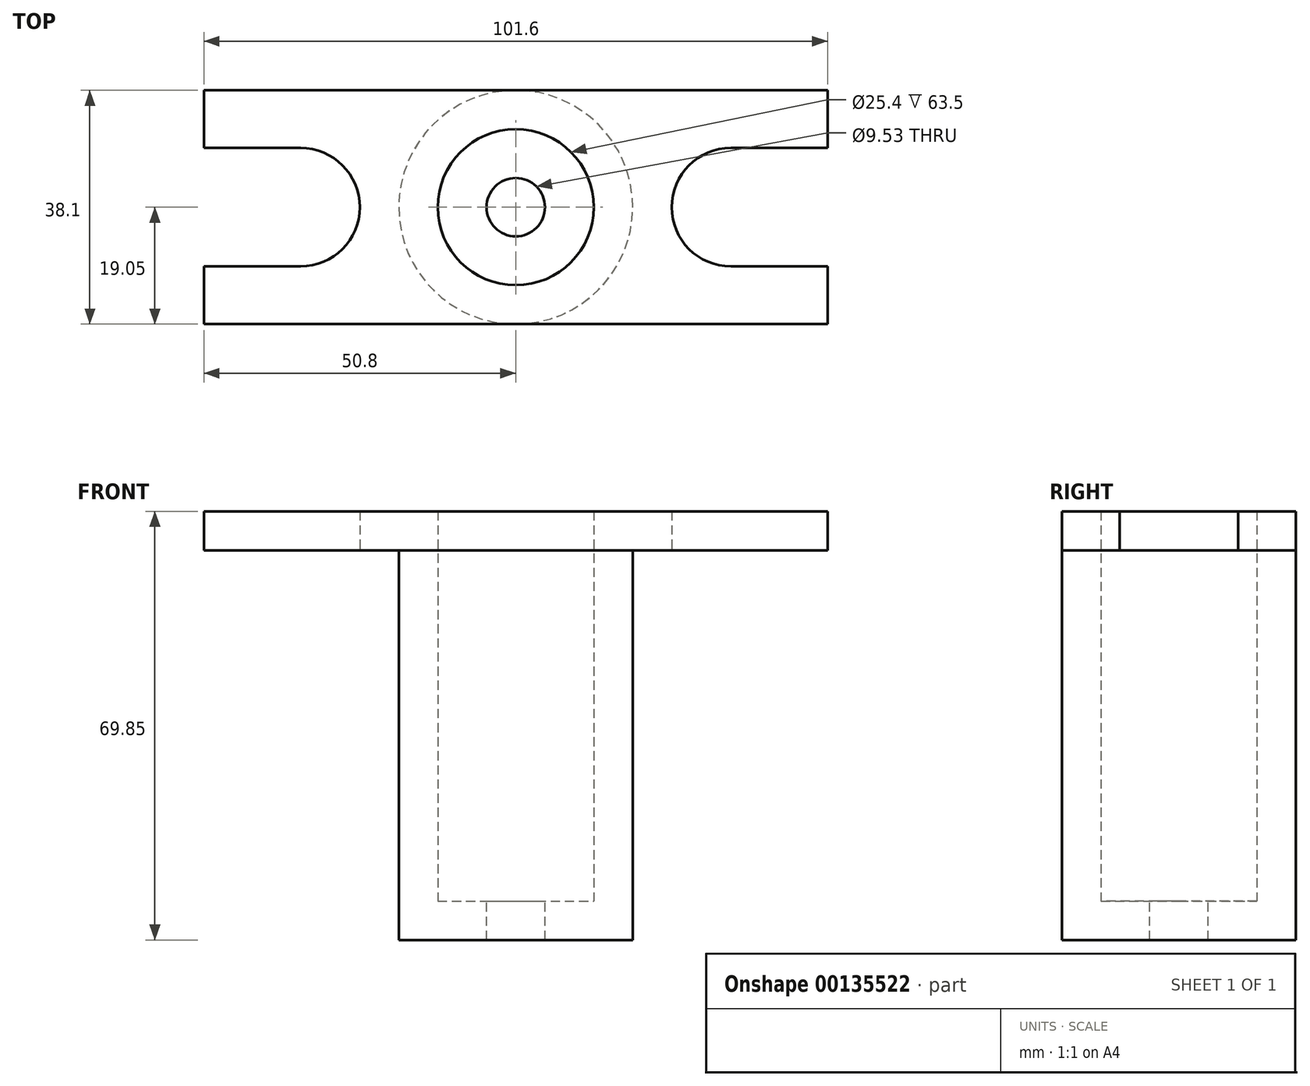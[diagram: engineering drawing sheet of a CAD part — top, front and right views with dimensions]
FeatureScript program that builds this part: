
annotation { "Feature Type Name" : "Feature", "Feature Type Description" : "" }
export const myFeature = defineFeature(function(context is Context, id is Id, definition is map)
    precondition{}
    {
        {
            var Q0;
            Q0=qCreatedBy(makeId("Top.planeOp"),FACE);
            var sketch = newSketch(context, id + "F0", { "sketchPlane" : qUnion([Q0])});
            skLineSegment(sketch, "E0.bottom", {"start": v(0, 0) * mm, "end": v(101.6, 0) * mm});
            skLineSegment(sketch, "E0.top", {"start": v(0, 38.1) * mm, "end": v(101.6, 38.1) * mm});
            skLineSegment(sketch, "E0.left", {"start": v(0, 0) * mm, "end": v(0, 9.4) * mm});
            skLineSegment(sketch, "E0.right", {"start": v(101.6, 0) * mm, "end": v(101.6, 9.4) * mm});
            skLineSegment(sketch, "E1", {"start": v(50.8, 38.1) * mm, "end": v(50.8, 0) * mm, "construction": true});
            skLineSegment(sketch, "E2", {"start": v(0, 19.05) * mm, "end": v(101.6, 19.05) * mm, "construction": true});
            skCircle(sketch, "E3", {"center": v(50.8, 19.05) * mm, "radius": 12.7 * mm});
            skCircle(sketch, "E4", {"center": v(50.8, 19.05) * mm, "radius": 19.05 * mm});
            skCircle(sketch, "E5", {"center": v(50.8, 19.05) * mm, "radius": 4.76 * mm});
            skLineSegment(sketch, "E6", {"start": v(101.6, 28.7) * mm, "end": v(85.85, 28.7) * mm});
            skLineSegment(sketch, "E7", {"start": v(101.6, 9.4) * mm, "end": v(85.85, 9.4) * mm});
            skArc(sketch, "E8", {"start": v(85.85, 28.7) * mm, "mid": v(76.2, 19.05) * mm, "end": v(85.85, 9.4) * mm});
            skLineSegment(sketch, "E9.MirrorCS", {"start": v(0, 28.7) * mm, "end": v(15.75, 28.7) * mm});
            skArc(sketch, "E10.MirrorCS", {"start": v(15.75, 28.7) * mm, "mid": v(25.4, 19.05) * mm, "end": v(15.75, 9.4) * mm});
            skLineSegment(sketch, "E11.MirrorCS", {"start": v(0, 9.4) * mm, "end": v(15.75, 9.4) * mm});
            skLineSegment(sketch, "E12.trimOffspring", {"start": v(0, 28.7) * mm, "end": v(0, 38.1) * mm});
            skLineSegment(sketch, "E13.trimOffspring", {"start": v(101.6, 28.7) * mm, "end": v(101.6, 38.1) * mm});
            skSolve(sketch);
        }
        {
            var Q0;
            Q0 = qSketchRegion(id + "F0", true);
            extrude(context, id + "F1", {"entities" : qUnion([Q0]), "depth" : 6.35 * mm});
        }
        {
            var Q0;
            Q0=makeQuery(id+"F0.imprint","IMPRINT",FACE,{"disambiguationData":[TD([[makeQuery(id+"F0.imprint","IMPRINT",EDGE,{"derivedFrom":sQuery(id+"F0.wireOp",EDGE,"E3")}),-1.0]])]});
            extrude(context, id + "F2", {"entities" : qUnion([Q0]), "operationType" : NewBodyOperationType.ADD, "oppositeDirection" : true, "depth" : 63.5 * mm});
        }
        {
            var Q0;
            Q0=makeQuery(id+"F2.opExtrude","CAP_FACE",FACE,{"disambiguationData":[OSD([sQuery(id+"F0.wireOp",EDGE,"E3"),sQuery(id+"F0.wireOp",EDGE,"E4")])],"isStart":false});
            var sketch = newSketch(context, id + "F3", { "sketchPlane" : qUnion([Q0])});
            skCircle(sketch, "E14.0", {"center": v(50.8, -19.05) * mm, "radius": 19.05 * mm});
            skSolve(sketch);
        }
        {
            var Q0;
            Q0 = qSketchRegion(id + "F3", true);
            extrude(context, id + "F4", {"entities" : qUnion([Q0]), "operationType" : NewBodyOperationType.ADD, "oppositeDirection" : true, "depth" : 6.35 * mm});
        }
        {
            var Q0;
            Q0=makeQuery(id+"F0.imprint","IMPRINT",FACE,{"disambiguationData":[TD([[makeQuery(id+"F0.imprint","IMPRINT",EDGE,{"derivedFrom":sQuery(id+"F0.wireOp",EDGE,"E5")}),1.0]])]});
            extrude(context, id + "F5", {"entities" : qUnion([Q0]), "operationType" : NewBodyOperationType.REMOVE, "endBound" : BoundingType.THROUGH_ALL, "oppositeDirection" : true, "depth" : 25.4 * mm});
        }
    });
